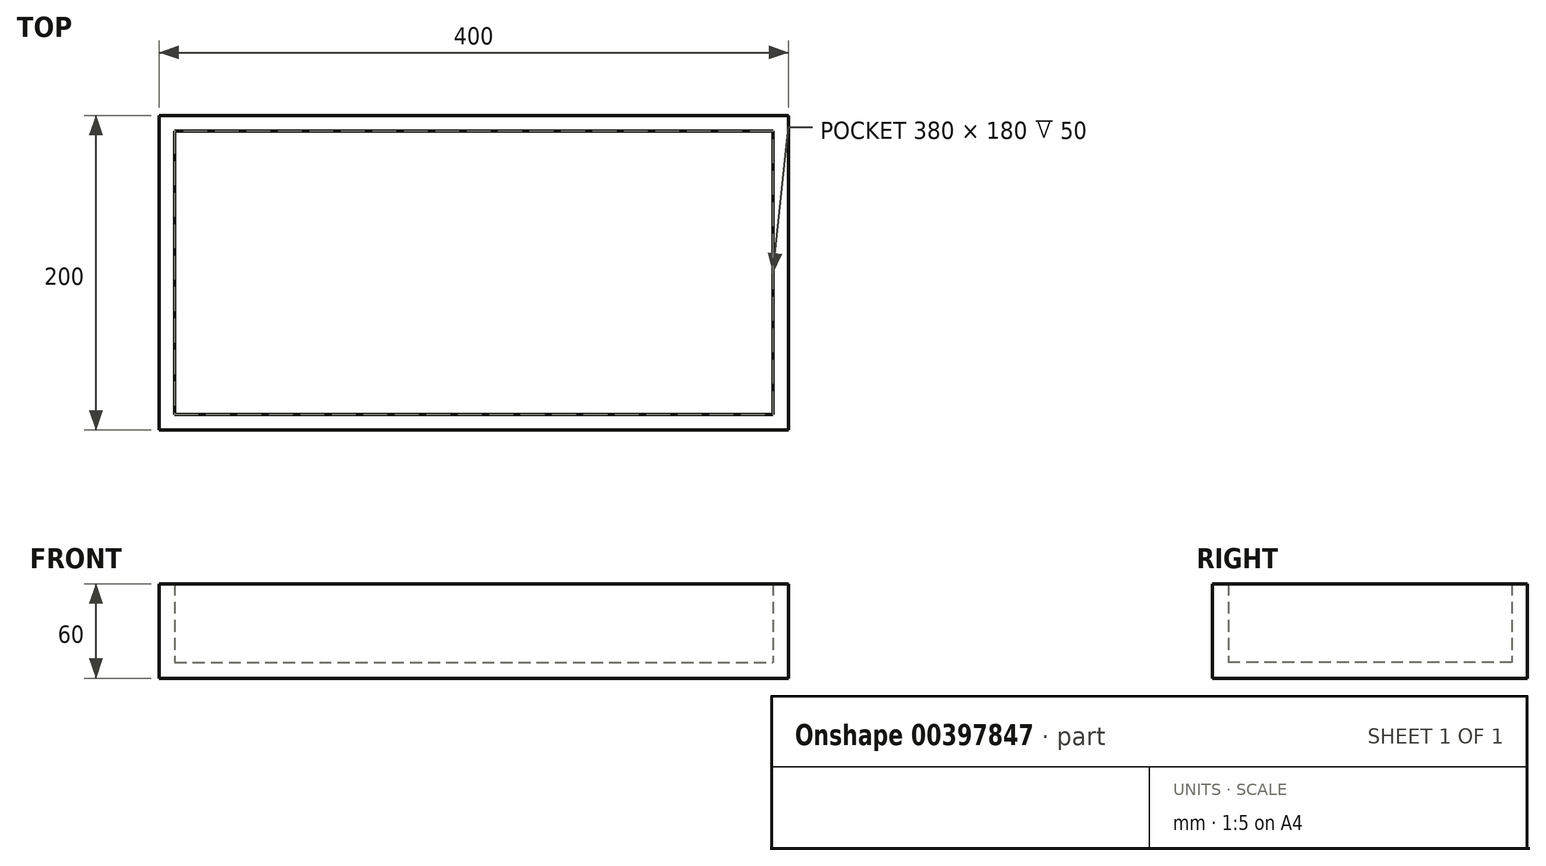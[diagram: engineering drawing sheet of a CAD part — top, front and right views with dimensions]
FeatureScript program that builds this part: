
annotation { "Feature Type Name" : "Feature", "Feature Type Description" : "" }
export const myFeature = defineFeature(function(context is Context, id is Id, definition is map)
    precondition{}
    {
        {
            var Q0;
            Q0=qCreatedBy(makeId("Top.planeOp"),FACE);
            var sketch = newSketch(context, id + "F0", { "sketchPlane" : qUnion([Q0])});
            skLineSegment(sketch, "E0.bottom", {"start": v(200, -100) * mm, "end": v(-200, -100) * mm});
            skLineSegment(sketch, "E0.top", {"start": v(200, 100) * mm, "end": v(-200, 100) * mm});
            skLineSegment(sketch, "E0.left", {"start": v(200, -100) * mm, "end": v(200, 100) * mm});
            skLineSegment(sketch, "E0.right", {"start": v(-200, -100) * mm, "end": v(-200, 100) * mm});
            skPoint(sketch, "E0.middle", {"position": v(0, 0) * mm});
            skSolve(sketch);
        }
        {
            var Q0;
            Q0 = qSketchRegion(id + "F0", true);
            extrude(context, id + "F1", {"entities" : qUnion([Q0]), "depth" : 10 * mm});
        }
        {
            var Q0;
            Q0=makeQuery(id+"F1.opExtrude","CAP_FACE",FACE,{"disambiguationData":[OSD([sQuery(id+"F0.wireOp",EDGE,"E0.bottom"),sQuery(id+"F0.wireOp",EDGE,"E0.top"),sQuery(id+"F0.wireOp",EDGE,"E0.left"),sQuery(id+"F0.wireOp",EDGE,"E0.right")])],"isStart":false});
            var sketch = newSketch(context, id + "F2", { "sketchPlane" : qUnion([Q0])});
            skLineSegment(sketch, "E1.bottom", {"start": v(-200, 100) * mm, "end": v(200, 100) * mm});
            skLineSegment(sketch, "E1.top", {"start": v(-200, -100) * mm, "end": v(200, -100) * mm});
            skLineSegment(sketch, "E1.left", {"start": v(-200, 100) * mm, "end": v(-200, -100) * mm});
            skLineSegment(sketch, "E1.right", {"start": v(200, 100) * mm, "end": v(200, -100) * mm});
            skLineSegment(sketch, "E2.0", {"start": v(-190, 90) * mm, "end": v(190, 90) * mm});
            skLineSegment(sketch, "E2.1", {"start": v(-190, 90) * mm, "end": v(-190, -90) * mm});
            skLineSegment(sketch, "E2.2", {"start": v(-190, -90) * mm, "end": v(190, -90) * mm});
            skLineSegment(sketch, "E2.3", {"start": v(190, 90) * mm, "end": v(190, -90) * mm});
            skSolve(sketch);
        }
        {
            var Q0;
            Q0 = qSketchRegion(id + "F2", true);
            extrude(context, id + "F3", {"entities" : qUnion([Q0]), "operationType" : NewBodyOperationType.ADD, "depth" : 50 * mm});
        }
    });
